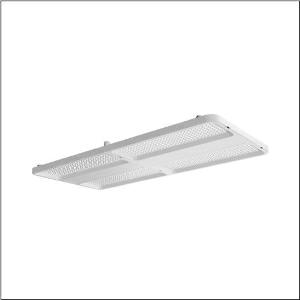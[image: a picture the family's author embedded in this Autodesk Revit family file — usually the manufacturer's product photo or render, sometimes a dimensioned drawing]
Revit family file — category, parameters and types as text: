
# Revit family: highbay_21_maxi_52hn11db4tea
name_source: partatom
category: Lighting Fixtures
units: mm (PartAtom-declared; Revit-internal decimal feet)

## family parameters
Cut with Voids When Loaded = No
Host = Face
Light Source = No
Part Type = Normal
Room Calculation Point = No
Round Connector Dimension = Use Diameter
Shared = No

## types (1)
- --- (1 x LED, 8350 lm, 44.8 W, 4000K)
    Apparent Load = 45 VA
    CIE Flux Codes = 89 97 99 100 100
    Color Rendering = 80
    Color Temperature = 4000K
    Default Elevation = 1800 mm
    Description = high bay luminaire Highbay 21 maxi; direct symmetric narrow distribution, light control with lens of PMMA; UGR ≤ 22 (X = 4H | Y = 8H | S = 0.25H | reflection values 70/50/20); luminous flux: 53.000lm; light colour: 840, colour temperature: 4000K, MacAdam ≤ 3 SDCM (initial), colour rendering: CRI > 80; luminous efficacy: 184,9lm/W; rated service life: 75.000h (L80) at AT= ta max; control: DALI 2; luminaire connection: 2x terminal, 5-pole, max. 2.5mm² with through-wiring: 1x feed-in / 1x feed-out (cable entry for two cables, Ø 8.5..13mm); mains connection: 230..240V, AC/DC 0/50..60Hz; connected load: 286,6W; protection rating (complete): IP66; insulation class (complete): insulation class I (protective earthing); protection symbol: D; impact resistance: IK08; certification: CE, ENEC, VDE, UKCA; luminaire for central battery installations according to EN 60598-2-22, internal wiring halogen-free; luminaire LABS conformity tested according to VDMA 24364:2018-05; Suitable for use in the food industry according to the specifications of IFS-Food, HACCP and/or BRC; housing frame of high-performance plastic PA6, matt traffic white (RAL 9016); cover of PMMA; dimension (LxWxH): 946 x 442 x 72mm; permissible operating ambient temperature: -40..+55°C (reducing of maximum allowable ambient temperature of 5°C with ceiling mounting); packaging unit: 1 piece; (delivery without accessories; please order mounting accessories separately)
    Height = 72 mm  [stored 0.23622 ft]
    Lamp = 1 x LED
    Lamp Light Flux = 8350 lm
    Lamp Power = 44.8 W
    Lamp count = 1
    Length = 946 mm
    Luminous efficacy = 186 lm/W
    Manufacturer = Siteco
    ModVariant = No
    Model = 52HN11DB4TEA
    Mounting Place = Ceiling
    Mounting Type = Pendant
    Number of Poles = 1
    OnlyDefault = Yes
    Power Factor = 1
    Product Name = Highbay 21 maxi
    Product group = high bay luminaire
    ProductGroupID = 902
    Protection Class = Protection class I
    Protection Degree = IP 66
    RLX_Detail_Level = 1
    RLX_Emergency_Light_Flux = 0 lm
    RLX_Emergency_Type = 0
    RLX_Emergency_Type_DB = No
    RlxData = <blob elided: 128593 chars, md5=d17734d3>
    Socket = socket
    Standby Power = 0 W
    System Light Flux = 8350 lm
    System Power = 45 W
    Type Comments = : DC mode (central or group accumulator) initial emergency light level
    Type Image = l_1363244.jpg
    URL = http://relux.com
    VarID = @adj_017761
    Voltage = 0 V
    Weight = 0.00 kg
    Width = 442 mm

note: [stored X ft] marks values corroborated as IEEE doubles in the binary element streams (Revit-internal decimal feet)

## geometry (parser evidence)
native form markers: Blend x4, Sweep x12
no freeform markers — native parametric forms only
